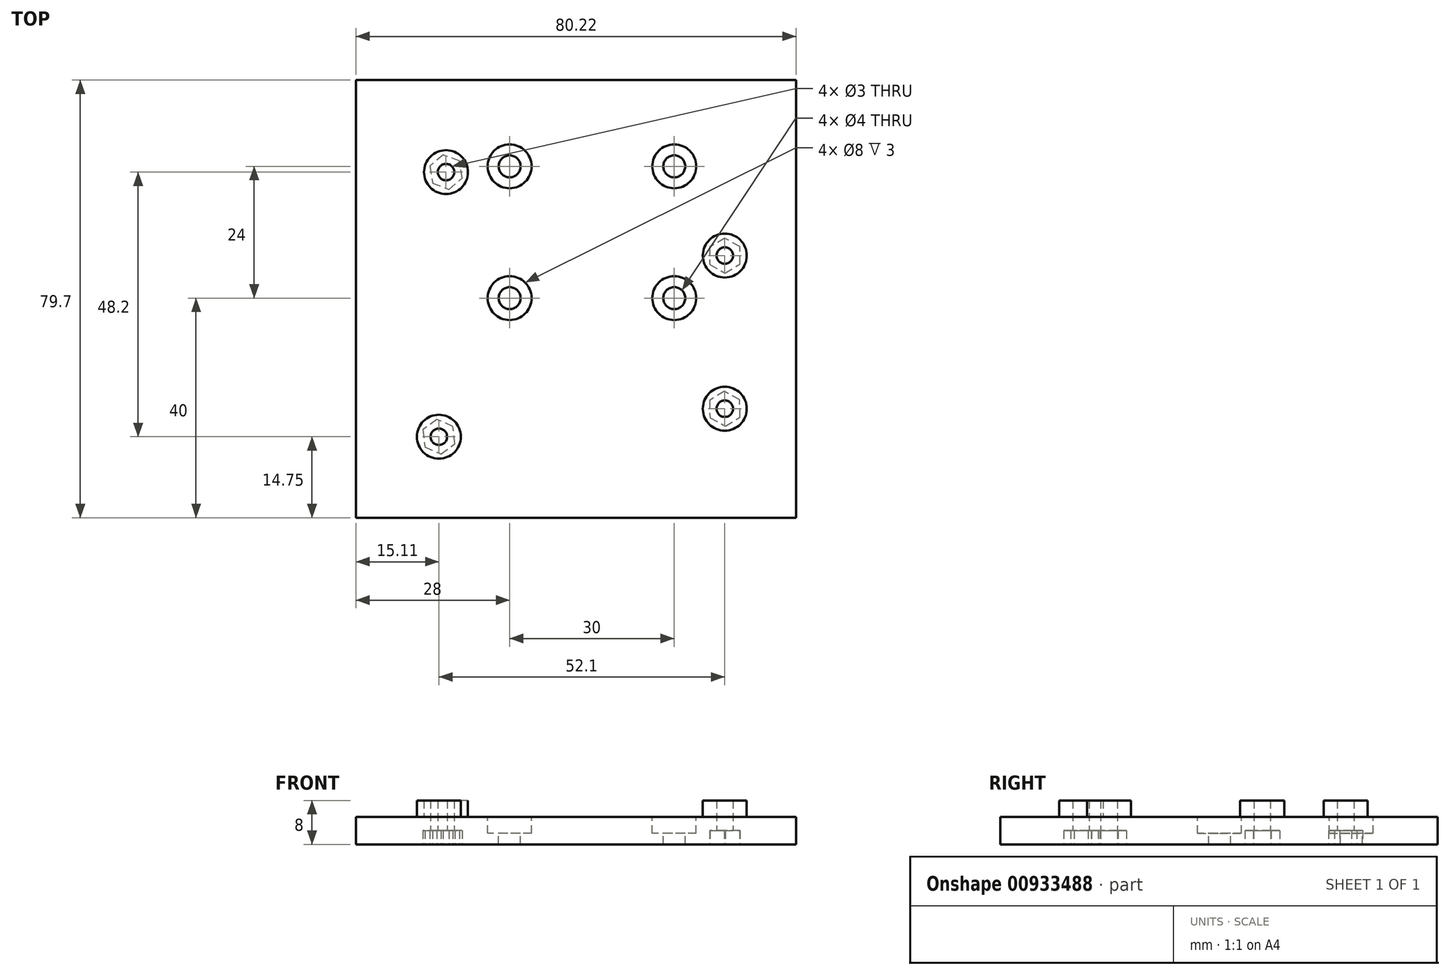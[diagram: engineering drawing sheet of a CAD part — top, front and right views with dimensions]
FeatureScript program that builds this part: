
annotation { "Feature Type Name" : "Feature", "Feature Type Description" : "" }
export const myFeature = defineFeature(function(context is Context, id is Id, definition is map)
    precondition{}
    {
        {
            var Q0;
            Q0=qCreatedBy(makeId("Top.planeOp"),FACE);
            var sketch = newSketch(context, id + "F0", { "sketchPlane" : qUnion([Q0])});
            skLineSegment(sketch, "E0.bottom", {"start": v(-35, 30) * mm, "end": v(35, 30) * mm});
            skLineSegment(sketch, "E0.top", {"start": v(-35, -30) * mm, "end": v(35, -30) * mm});
            skLineSegment(sketch, "E0.left", {"start": v(-35, 30) * mm, "end": v(-35, -30) * mm});
            skLineSegment(sketch, "E0.right", {"start": v(35, 30) * mm, "end": v(35, -30) * mm});
            skPoint(sketch, "E0.middle", {"position": v(0, 0) * mm});
            skSolve(sketch);
        }
        {
            var Q0;
            Q0 = qSketchRegion(id + "F0", true);
            extrude(context, id + "F1", {"entities" : qUnion([Q0]), "depth" : 5 * mm, "offsetDistance" : 25 * mm});
        }
        {
            var Q0;
            Q0=makeQuery(id+"F1.opExtrude","CAP_FACE",FACE,{"disambiguationData":[OSD([sQuery(id+"F0.wireOp",EDGE,"E0.bottom"),sQuery(id+"F0.wireOp",EDGE,"E0.top"),sQuery(id+"F0.wireOp",EDGE,"E0.left"),sQuery(id+"F0.wireOp",EDGE,"E0.right")])],"isStart":false});
            var sketch = newSketch(context, id + "F2", { "sketchPlane" : qUnion([Q0])});
            skCircle(sketch, "E1", {"center": v(-23.7, 23.1) * mm, "radius": 4 * mm});
            skCircle(sketch, "E2", {"center": v(-25, -25.1) * mm, "radius": 4 * mm});
            skCircle(sketch, "E3", {"center": v(27.1, 7.9) * mm, "radius": 4 * mm});
            skCircle(sketch, "E4", {"center": v(27.1, -20) * mm, "radius": 4 * mm});
            skSolve(sketch);
        }
        {
            var Q0;
            Q0 = qSketchRegion(id + "F2", true);
            extrude(context, id + "F3", {"entities" : qUnion([Q0]), "operationType" : NewBodyOperationType.ADD, "depth" : 3 * mm, "offsetDistance" : 25 * mm});
        }
        {
            var Q0;
            Q0=makeQuery(id+"F1.opExtrude","CAP_FACE",FACE,{"disambiguationData":[OSD([sQuery(id+"F0.wireOp",EDGE,"E0.bottom"),sQuery(id+"F0.wireOp",EDGE,"E0.top"),sQuery(id+"F0.wireOp",EDGE,"E0.left"),sQuery(id+"F0.wireOp",EDGE,"E0.right")])],"isStart":false});
            var sketch = newSketch(context, id + "F4", { "sketchPlane" : qUnion([Q0])});
            skCircle(sketch, "E5", {"center": v(-23.7, 23.1) * mm, "radius": 1.5 * mm});
            skCircle(sketch, "E6", {"center": v(27.1, 7.9) * mm, "radius": 1.5 * mm});
            skCircle(sketch, "E7", {"center": v(27.1, -20) * mm, "radius": 1.5 * mm});
            skCircle(sketch, "E8", {"center": v(-25, -25.1) * mm, "radius": 1.5 * mm});
            skSolve(sketch);
        }
        {
            var Q0;
            Q0 = qSketchRegion(id + "F4", true);
            extrude(context, id + "F5", {"entities" : qUnion([Q0]), "operationType" : NewBodyOperationType.REMOVE, "endBound" : BoundingType.THROUGH_ALL, "depth" : 5 * mm, "offsetDistance" : 25 * mm, "hasSecondDirection" : true, "secondDirectionOppositeDirection" : true, "secondDirectionDepth" : 5 * mm});
        }
        {
            var Q0;
            Q0=makeQuery(id+"F1.opExtrude","SWEPT_FACE",FACE,{"disambiguationData":[OSD([sQuery(id+"F0.wireOp",EDGE,"E0.top")])]});
            extrude(context, id + "F6", {"entities" : qUnion([Q0]), "operationType" : NewBodyOperationType.ADD, "depth" : 9.85 * mm, "offsetDistance" : 25 * mm});
        }
        {
            var Q0;
            Q0=makeQuery(id+"F1.opExtrude","SWEPT_FACE",FACE,{"disambiguationData":[OSD([sQuery(id+"F0.wireOp",EDGE,"E0.bottom")])]});
            extrude(context, id + "F7", {"entities" : qUnion([Q0]), "operationType" : NewBodyOperationType.ADD, "depth" : 9.85 * mm, "offsetDistance" : 25 * mm});
        }
        {
            var Q0;
            {var subQ0=sQuery(id+"F0.wireOp",EDGE,"E0.right");Q0=makeQuery(id+"F7.boolean.opBoolean","MERGE",FACE,{"derivedFrom":[makeQuery(id+"F6.boolean.opBoolean","MERGE",FACE,{"derivedFrom":[makeQuery(id+"F1.opExtrude","SWEPT_FACE",FACE,{"disambiguationData":[OSD([subQ0])]}),makeQuery(id+"F6.opExtrude","SWEPT_FACE",FACE,{"disambiguationData":[OSD([sQuery(id+"F0.wireOp",EDGE,"E0.top"),subQ0])]})]}),makeQuery(id+"F7.opExtrude","SWEPT_FACE",FACE,{"disambiguationData":[OSD([sQuery(id+"F0.wireOp",EDGE,"E0.bottom"),subQ0])]})]});}
            extrude(context, id + "F8", {"entities" : qUnion([Q0]), "operationType" : NewBodyOperationType.ADD, "depth" : 5.11 * mm, "offsetDistance" : 25 * mm});
        }
        {
            var Q0;
            {var subQ0=sQuery(id+"F0.wireOp",EDGE,"E0.left");Q0=makeQuery(id+"F7.boolean.opBoolean","MERGE",FACE,{"derivedFrom":[makeQuery(id+"F6.boolean.opBoolean","MERGE",FACE,{"derivedFrom":[makeQuery(id+"F1.opExtrude","SWEPT_FACE",FACE,{"disambiguationData":[OSD([subQ0])]}),makeQuery(id+"F6.opExtrude","SWEPT_FACE",FACE,{"disambiguationData":[OSD([sQuery(id+"F0.wireOp",EDGE,"E0.top"),subQ0])]})]}),makeQuery(id+"F7.opExtrude","SWEPT_FACE",FACE,{"disambiguationData":[OSD([sQuery(id+"F0.wireOp",EDGE,"E0.bottom"),subQ0])]})]});}
            extrude(context, id + "F9", {"entities" : qUnion([Q0]), "operationType" : NewBodyOperationType.ADD, "depth" : 5.11 * mm, "offsetDistance" : 25 * mm});
        }
        {
            var Q0;
            {var subQ0=sQuery(id+"F0.wireOp",EDGE,"E0.left");var subQ1=sQuery(id+"F0.wireOp",EDGE,"E0.bottom");var subQ2=sQuery(id+"F0.wireOp",EDGE,"E0.top");var subQ3=sQuery(id+"F0.wireOp",EDGE,"E0.right");Q0=makeQuery(id+"F9.boolean.opBoolean","MERGE",FACE,{"derivedFrom":[makeQuery(id+"F8.boolean.opBoolean","MERGE",FACE,{"derivedFrom":[makeQuery(id+"F7.boolean.opBoolean","MERGE",FACE,{"derivedFrom":[makeQuery(id+"F6.boolean.opBoolean","MERGE",FACE,{"derivedFrom":[makeQuery(id+"F1.opExtrude","CAP_FACE",FACE,{"disambiguationData":[OSD([subQ1,subQ2,subQ0,subQ3])],"isStart":false}),makeQuery(id+"F6.opExtrude","SWEPT_FACE",FACE,{"disambiguationData":[OSD([subQ2]),TDD([makeQuery(id+"F1.opExtrude","CAP_EDGE",EDGE,{"disambiguationData":[OSD([subQ2])],"isStart":false})])]})]}),makeQuery(id+"F7.opExtrude","SWEPT_FACE",FACE,{"disambiguationData":[OSD([subQ1]),TDD([makeQuery(id+"F1.opExtrude","CAP_EDGE",EDGE,{"disambiguationData":[OSD([subQ1])],"isStart":false})])]})]}),makeQuery(id+"F8.opExtrude","SWEPT_FACE",FACE,{"disambiguationData":[OSD([subQ1,subQ2,subQ3]),TDD([makeQuery(id+"F7.boolean.opBoolean","MERGE",EDGE,{"derivedFrom":[makeQuery(id+"F6.boolean.opBoolean","MERGE",EDGE,{"derivedFrom":[makeQuery(id+"F1.opExtrude","CAP_EDGE",EDGE,{"disambiguationData":[OSD([subQ3])],"isStart":false}),makeQuery(id+"F6.opExtrude","SWEPT_EDGE",EDGE,{"disambiguationData":[OSD([subQ2,subQ3]),TDD([makeQuery(id+"F1.opExtrude","CAP_VERTEX",VERTEX,{"disambiguationData":[OSD([subQ2,subQ3])],"isStart":false})])]})]}),makeQuery(id+"F7.opExtrude","SWEPT_EDGE",EDGE,{"disambiguationData":[OSD([subQ1,subQ3]),TDD([makeQuery(id+"F1.opExtrude","CAP_VERTEX",VERTEX,{"disambiguationData":[OSD([subQ1,subQ3])],"isStart":false})])]})]})])]})]}),makeQuery(id+"F9.opExtrude","SWEPT_FACE",FACE,{"disambiguationData":[OSD([subQ1,subQ2,subQ0]),TDD([makeQuery(id+"F7.boolean.opBoolean","MERGE",EDGE,{"derivedFrom":[makeQuery(id+"F6.boolean.opBoolean","MERGE",EDGE,{"derivedFrom":[makeQuery(id+"F1.opExtrude","CAP_EDGE",EDGE,{"disambiguationData":[OSD([subQ0])],"isStart":false}),makeQuery(id+"F6.opExtrude","SWEPT_EDGE",EDGE,{"disambiguationData":[OSD([subQ2,subQ0]),TDD([makeQuery(id+"F1.opExtrude","CAP_VERTEX",VERTEX,{"disambiguationData":[OSD([subQ2,subQ0])],"isStart":false})])]})]}),makeQuery(id+"F7.opExtrude","SWEPT_EDGE",EDGE,{"disambiguationData":[OSD([subQ1,subQ0]),TDD([makeQuery(id+"F1.opExtrude","CAP_VERTEX",VERTEX,{"disambiguationData":[OSD([subQ1,subQ0])],"isStart":false})])]})]})])]})]});}
            var sketch = newSketch(context, id + "F10", { "sketchPlane" : qUnion([Q0])});
            skCircle(sketch, "E9", {"center": v(-12.11, 0.15) * mm, "radius": 2 * mm});
            skCircle(sketch, "E10", {"center": v(-12.11, 24.15) * mm, "radius": 2 * mm});
            skCircle(sketch, "E11", {"center": v(17.89, 24.15) * mm, "radius": 2 * mm});
            skCircle(sketch, "E12", {"center": v(17.89, 0.15) * mm, "radius": 2 * mm});
            skSolve(sketch);
        }
        {
            var Q0;
            Q0 = qSketchRegion(id + "F10", true);
            extrude(context, id + "F11", {"entities" : qUnion([Q0]), "operationType" : NewBodyOperationType.REMOVE, "oppositeDirection" : true, "depth" : 5 * mm, "offsetDistance" : 25 * mm});
        }
        {
            var Q0;
            {var subQ0=sQuery(id+"F0.wireOp",EDGE,"E0.left");var subQ1=sQuery(id+"F0.wireOp",EDGE,"E0.bottom");var subQ2=sQuery(id+"F0.wireOp",EDGE,"E0.top");var subQ3=sQuery(id+"F0.wireOp",EDGE,"E0.right");Q0=makeQuery(id+"F9.boolean.opBoolean","MERGE",FACE,{"derivedFrom":[makeQuery(id+"F8.boolean.opBoolean","MERGE",FACE,{"derivedFrom":[makeQuery(id+"F7.boolean.opBoolean","MERGE",FACE,{"derivedFrom":[makeQuery(id+"F6.boolean.opBoolean","MERGE",FACE,{"derivedFrom":[makeQuery(id+"F1.opExtrude","CAP_FACE",FACE,{"disambiguationData":[OSD([subQ1,subQ2,subQ0,subQ3])],"isStart":false}),makeQuery(id+"F6.opExtrude","SWEPT_FACE",FACE,{"disambiguationData":[OSD([subQ2]),TDD([makeQuery(id+"F1.opExtrude","CAP_EDGE",EDGE,{"disambiguationData":[OSD([subQ2])],"isStart":false})])]})]}),makeQuery(id+"F7.opExtrude","SWEPT_FACE",FACE,{"disambiguationData":[OSD([subQ1]),TDD([makeQuery(id+"F1.opExtrude","CAP_EDGE",EDGE,{"disambiguationData":[OSD([subQ1])],"isStart":false})])]})]}),makeQuery(id+"F8.opExtrude","SWEPT_FACE",FACE,{"disambiguationData":[OSD([subQ1,subQ2,subQ3]),TDD([makeQuery(id+"F7.boolean.opBoolean","MERGE",EDGE,{"derivedFrom":[makeQuery(id+"F6.boolean.opBoolean","MERGE",EDGE,{"derivedFrom":[makeQuery(id+"F1.opExtrude","CAP_EDGE",EDGE,{"disambiguationData":[OSD([subQ3])],"isStart":false}),makeQuery(id+"F6.opExtrude","SWEPT_EDGE",EDGE,{"disambiguationData":[OSD([subQ2,subQ3]),TDD([makeQuery(id+"F1.opExtrude","CAP_VERTEX",VERTEX,{"disambiguationData":[OSD([subQ2,subQ3])],"isStart":false})])]})]}),makeQuery(id+"F7.opExtrude","SWEPT_EDGE",EDGE,{"disambiguationData":[OSD([subQ1,subQ3]),TDD([makeQuery(id+"F1.opExtrude","CAP_VERTEX",VERTEX,{"disambiguationData":[OSD([subQ1,subQ3])],"isStart":false})])]})]})])]})]}),makeQuery(id+"F9.opExtrude","SWEPT_FACE",FACE,{"disambiguationData":[OSD([subQ1,subQ2,subQ0]),TDD([makeQuery(id+"F7.boolean.opBoolean","MERGE",EDGE,{"derivedFrom":[makeQuery(id+"F6.boolean.opBoolean","MERGE",EDGE,{"derivedFrom":[makeQuery(id+"F1.opExtrude","CAP_EDGE",EDGE,{"disambiguationData":[OSD([subQ0])],"isStart":false}),makeQuery(id+"F6.opExtrude","SWEPT_EDGE",EDGE,{"disambiguationData":[OSD([subQ2,subQ0]),TDD([makeQuery(id+"F1.opExtrude","CAP_VERTEX",VERTEX,{"disambiguationData":[OSD([subQ2,subQ0])],"isStart":false})])]})]}),makeQuery(id+"F7.opExtrude","SWEPT_EDGE",EDGE,{"disambiguationData":[OSD([subQ1,subQ0]),TDD([makeQuery(id+"F1.opExtrude","CAP_VERTEX",VERTEX,{"disambiguationData":[OSD([subQ1,subQ0])],"isStart":false})])]})]})])]})]});}
            var sketch = newSketch(context, id + "F12", { "sketchPlane" : qUnion([Q0])});
            skCircle(sketch, "E13", {"center": v(-12.11, 0.15) * mm, "radius": 4 * mm});
            skCircle(sketch, "E14", {"center": v(-12.11, 24.15) * mm, "radius": 4 * mm});
            skCircle(sketch, "E15", {"center": v(17.89, 24.15) * mm, "radius": 4 * mm});
            skCircle(sketch, "E16", {"center": v(17.89, 0.15) * mm, "radius": 4 * mm});
            skSolve(sketch);
        }
        {
            var Q0;
            Q0 = qSketchRegion(id + "F12", true);
            extrude(context, id + "F13", {"entities" : qUnion([Q0]), "operationType" : NewBodyOperationType.REMOVE, "oppositeDirection" : true, "depth" : 3 * mm, "offsetDistance" : 25 * mm});
        }
        {
            var Q0;
            {var subQ0=sQuery(id+"F0.wireOp",EDGE,"E0.left");var subQ1=sQuery(id+"F0.wireOp",EDGE,"E0.bottom");var subQ2=sQuery(id+"F0.wireOp",EDGE,"E0.top");var subQ3=sQuery(id+"F0.wireOp",EDGE,"E0.right");Q0=makeQuery(id+"F9.boolean.opBoolean","MERGE",FACE,{"derivedFrom":[makeQuery(id+"F8.boolean.opBoolean","MERGE",FACE,{"derivedFrom":[makeQuery(id+"F7.boolean.opBoolean","MERGE",FACE,{"derivedFrom":[makeQuery(id+"F6.boolean.opBoolean","MERGE",FACE,{"derivedFrom":[makeQuery(id+"F1.opExtrude","CAP_FACE",FACE,{"disambiguationData":[OSD([subQ1,subQ2,subQ0,subQ3])],"isStart":true}),makeQuery(id+"F6.opExtrude","SWEPT_FACE",FACE,{"disambiguationData":[OSD([subQ2]),TDD([makeQuery(id+"F1.opExtrude","CAP_EDGE",EDGE,{"disambiguationData":[OSD([subQ2])],"isStart":true})])]})]}),makeQuery(id+"F7.opExtrude","SWEPT_FACE",FACE,{"disambiguationData":[OSD([subQ1]),TDD([makeQuery(id+"F1.opExtrude","CAP_EDGE",EDGE,{"disambiguationData":[OSD([subQ1])],"isStart":true})])]})]}),makeQuery(id+"F8.opExtrude","SWEPT_FACE",FACE,{"disambiguationData":[OSD([subQ1,subQ2,subQ3]),TDD([makeQuery(id+"F7.boolean.opBoolean","MERGE",EDGE,{"derivedFrom":[makeQuery(id+"F6.boolean.opBoolean","MERGE",EDGE,{"derivedFrom":[makeQuery(id+"F1.opExtrude","CAP_EDGE",EDGE,{"disambiguationData":[OSD([subQ3])],"isStart":true}),makeQuery(id+"F6.opExtrude","SWEPT_EDGE",EDGE,{"disambiguationData":[OSD([subQ2,subQ3]),TDD([makeQuery(id+"F1.opExtrude","CAP_VERTEX",VERTEX,{"disambiguationData":[OSD([subQ2,subQ3])],"isStart":true})])]})]}),makeQuery(id+"F7.opExtrude","SWEPT_EDGE",EDGE,{"disambiguationData":[OSD([subQ1,subQ3]),TDD([makeQuery(id+"F1.opExtrude","CAP_VERTEX",VERTEX,{"disambiguationData":[OSD([subQ1,subQ3])],"isStart":true})])]})]})])]})]}),makeQuery(id+"F9.opExtrude","SWEPT_FACE",FACE,{"disambiguationData":[OSD([subQ1,subQ2,subQ0]),TDD([makeQuery(id+"F7.boolean.opBoolean","MERGE",EDGE,{"derivedFrom":[makeQuery(id+"F6.boolean.opBoolean","MERGE",EDGE,{"derivedFrom":[makeQuery(id+"F1.opExtrude","CAP_EDGE",EDGE,{"disambiguationData":[OSD([subQ0])],"isStart":true}),makeQuery(id+"F6.opExtrude","SWEPT_EDGE",EDGE,{"disambiguationData":[OSD([subQ2,subQ0]),TDD([makeQuery(id+"F1.opExtrude","CAP_VERTEX",VERTEX,{"disambiguationData":[OSD([subQ2,subQ0])],"isStart":true})])]})]}),makeQuery(id+"F7.opExtrude","SWEPT_EDGE",EDGE,{"disambiguationData":[OSD([subQ1,subQ0]),TDD([makeQuery(id+"F1.opExtrude","CAP_VERTEX",VERTEX,{"disambiguationData":[OSD([subQ1,subQ0])],"isStart":true})])]})]})])]})]});}
            var sketch = newSketch(context, id + "F14", { "sketchPlane" : qUnion([Q0])});
            skCircle(sketch, "E17.cCircle", {"center": v(-25, 25.1) * mm, "radius": 2.75 * mm, "construction": true});
            skLineSegment(sketch, "E17.0", {"start": v(-27.56, 26.98) * mm, "end": v(-24.65, 28.26) * mm});
            skLineSegment(sketch, "E17.1", {"start": v(-24.65, 28.26) * mm, "end": v(-22.1, 26.37) * mm});
            skLineSegment(sketch, "E17.2", {"start": v(-22.1, 26.37) * mm, "end": v(-22.44, 23.22) * mm});
            skLineSegment(sketch, "E17.3", {"start": v(-22.44, 23.22) * mm, "end": v(-25.35, 21.94) * mm});
            skLineSegment(sketch, "E17.4", {"start": v(-25.35, 21.94) * mm, "end": v(-27.9, 23.83) * mm});
            skLineSegment(sketch, "E17.5", {"start": v(-27.9, 23.83) * mm, "end": v(-27.56, 26.98) * mm});
            skPoint(sketch, "E17.0.midPoint", {"position": v(-26.1, 27.62) * mm});
            skCircle(sketch, "E18.cCircle", {"center": v(27.1, 20) * mm, "radius": 2.75 * mm, "construction": true});
            skLineSegment(sketch, "E18.0", {"start": v(24.4, 21.66) * mm, "end": v(27.18, 23.17) * mm});
            skLineSegment(sketch, "E18.1", {"start": v(27.18, 23.17) * mm, "end": v(29.9, 21.52) * mm});
            skLineSegment(sketch, "E18.2", {"start": v(29.9, 21.52) * mm, "end": v(29.8, 18.34) * mm});
            skLineSegment(sketch, "E18.3", {"start": v(29.8, 18.34) * mm, "end": v(27.02, 16.83) * mm});
            skLineSegment(sketch, "E18.4", {"start": v(27.02, 16.83) * mm, "end": v(24.3, 18.48) * mm});
            skLineSegment(sketch, "E18.5", {"start": v(24.3, 18.48) * mm, "end": v(24.4, 21.66) * mm});
            skPoint(sketch, "E18.0.midPoint", {"position": v(25.79, 22.42) * mm});
            skCircle(sketch, "E19.cCircle", {"center": v(27.1, -7.9) * mm, "radius": 2.75 * mm, "construction": true});
            skLineSegment(sketch, "E19.0", {"start": v(24.36, -6.3) * mm, "end": v(27.12, -4.72) * mm});
            skLineSegment(sketch, "E19.1", {"start": v(27.12, -4.72) * mm, "end": v(29.86, -6.33) * mm});
            skLineSegment(sketch, "E19.2", {"start": v(29.86, -6.33) * mm, "end": v(29.84, -9.5) * mm});
            skLineSegment(sketch, "E19.3", {"start": v(29.84, -9.5) * mm, "end": v(27.08, -11.08) * mm});
            skLineSegment(sketch, "E19.4", {"start": v(27.08, -11.08) * mm, "end": v(24.34, -9.47) * mm});
            skLineSegment(sketch, "E19.5", {"start": v(24.34, -9.47) * mm, "end": v(24.36, -6.3) * mm});
            skPoint(sketch, "E19.0.midPoint", {"position": v(25.74, -5.51) * mm});
            skCircle(sketch, "E20.cCircle", {"center": v(-23.7, -23.1) * mm, "radius": 2.75 * mm, "construction": true});
            skLineSegment(sketch, "E20.0", {"start": v(-26.14, -21.06) * mm, "end": v(-23.16, -19.97) * mm});
            skLineSegment(sketch, "E20.1", {"start": v(-23.16, -19.97) * mm, "end": v(-20.72, -22) * mm});
            skLineSegment(sketch, "E20.2", {"start": v(-20.72, -22) * mm, "end": v(-21.26, -25.14) * mm});
            skLineSegment(sketch, "E20.3", {"start": v(-21.26, -25.14) * mm, "end": v(-24.24, -26.23) * mm});
            skLineSegment(sketch, "E20.4", {"start": v(-24.24, -26.23) * mm, "end": v(-26.68, -24.2) * mm});
            skLineSegment(sketch, "E20.5", {"start": v(-26.68, -24.2) * mm, "end": v(-26.14, -21.06) * mm});
            skPoint(sketch, "E20.0.midPoint", {"position": v(-24.65, -20.52) * mm});
            skSolve(sketch);
        }
        {
            var Q0;
            Q0 = qSketchRegion(id + "F14", true);
            extrude(context, id + "F15", {"entities" : qUnion([Q0]), "operationType" : NewBodyOperationType.REMOVE, "oppositeDirection" : true, "depth" : 2.5 * mm, "offsetDistance" : 25 * mm});
        }
    });
